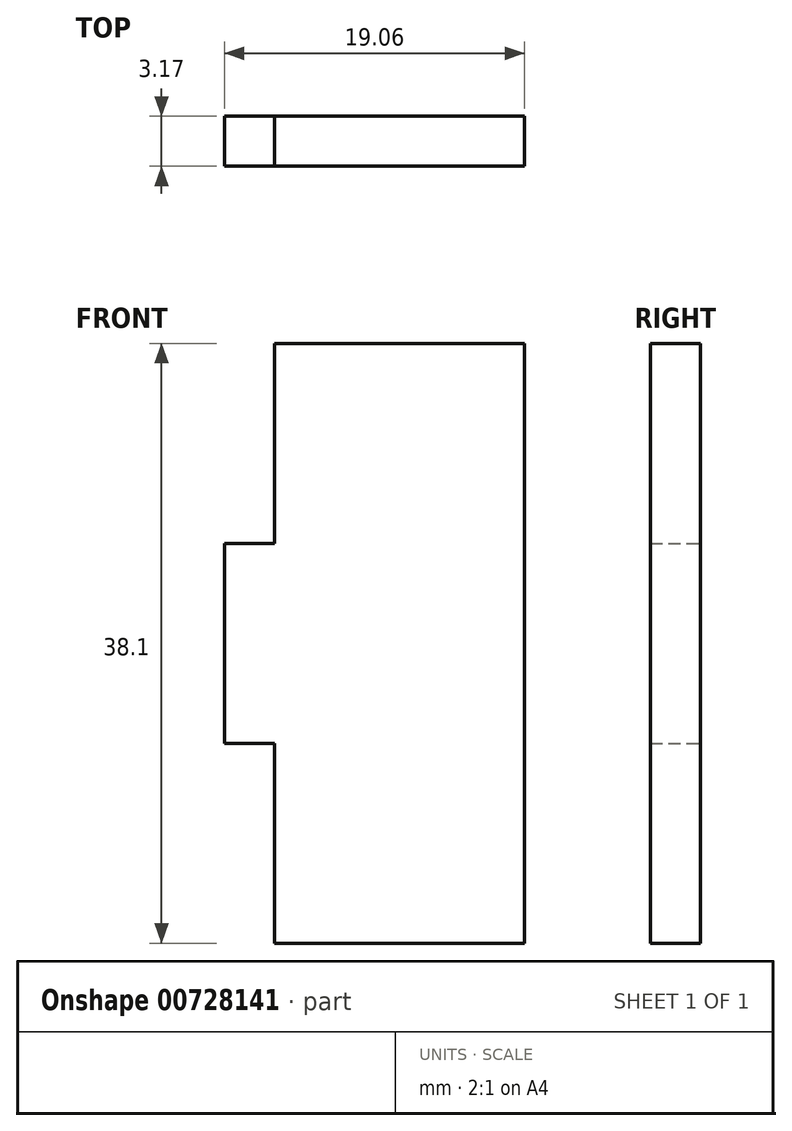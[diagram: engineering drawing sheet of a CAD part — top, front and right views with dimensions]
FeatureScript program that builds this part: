
annotation { "Feature Type Name" : "Feature", "Feature Type Description" : "" }
export const myFeature = defineFeature(function(context is Context, id is Id, definition is map)
    precondition{}
    {
        {
            var Q0;
            Q0=qCreatedBy(makeId("Front.planeOp"),FACE);
            var sketch = newSketch(context, id + "F0", { "sketchPlane" : qUnion([Q0])});
            skLineSegment(sketch, "E0.bottom", {"start": v(9.52, 31.75) * mm, "end": v(-9.53, 31.75) * mm});
            skLineSegment(sketch, "E0.top", {"start": v(9.52, -31.75) * mm, "end": v(-9.53, -31.75) * mm});
            skLineSegment(sketch, "E0.left", {"start": v(9.52, 31.75) * mm, "end": v(9.52, -31.75) * mm});
            skLineSegment(sketch, "E0.right", {"start": v(-9.53, 31.75) * mm, "end": v(-9.53, -31.75) * mm});
            skPoint(sketch, "E0.middle", {"position": v(0, 0) * mm});
            skLineSegment(sketch, "E1.bottom", {"start": v(-9.53, -31.75) * mm, "end": v(-6.35, -31.75) * mm});
            skLineSegment(sketch, "E1.top", {"start": v(-9.53, 31.75) * mm, "end": v(-6.35, 31.75) * mm});
            skLineSegment(sketch, "E1.left", {"start": v(-9.53, -31.75) * mm, "end": v(-9.53, 31.75) * mm});
            skLineSegment(sketch, "E1.right", {"start": v(-6.35, -31.75) * mm, "end": v(-6.35, 31.75) * mm});
            skLineSegment(sketch, "E2", {"start": v(-9.53, 19.05) * mm, "end": v(-6.35, 19.05) * mm});
            skLineSegment(sketch, "E3", {"start": v(-9.53, 6.35) * mm, "end": v(-6.35, 6.35) * mm});
            skLineSegment(sketch, "E4", {"start": v(-9.53, -6.35) * mm, "end": v(-6.35, -6.35) * mm});
            skLineSegment(sketch, "E5", {"start": v(-9.52, -19.05) * mm, "end": v(-6.35, -19.05) * mm});
            skLineSegment(sketch, "E6", {"start": v(-6.35, -19.05) * mm, "end": v(9.52, -19.05) * mm});
            skLineSegment(sketch, "E7", {"start": v(-6.35, 19.05) * mm, "end": v(9.52, 19.05) * mm});
            skSolve(sketch);
        }
        {
            var Q0;
            {var subQ0=sQuery(id+"F0.wireOp",EDGE,"E3");Q0=makeQuery(id+"F0.imprint","IMPRINT",FACE,{"disambiguationData":[TD([[makeQuery(id+"F0.imprint","IMPRINT",EDGE,{"derivedFrom":subQ0}),-1.0]])]});}
            var Q1;
            {var subQ4=sQuery(id+"F0.wireOp",EDGE,"E6");Q1=makeQuery(id+"F0.imprint","IMPRINT",FACE,{"disambiguationData":[TD([[makeQuery(id+"F0.imprint","IMPRINT",EDGE,{"derivedFrom":subQ4}),1.0]])]});}
            extrude(context, id + "F1", {"entities" : qUnion([Q0, Q1]), "depth" : 3.17 * mm, "offsetDistance" : 25.4 * mm});
        }
    });
